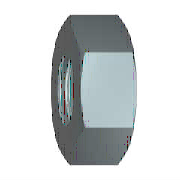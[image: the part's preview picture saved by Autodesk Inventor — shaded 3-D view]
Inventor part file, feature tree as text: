
AUTODESK INVENTOR PART (.ipt)
format: ipt  version: 2017 (Build 210142000, 142)  size: 175,104 bytes
history: native  units: mm (DEFAULTED — no unit token found)
features: sketch x3, chamfer x1, hole x1, other x1, plane x1
ambient origin geometry x7: Origin, YZ Plane, XZ Plane, X Axis, Y Axis, Z Axis, Center Point
bodies: Solid1 (feature_tree), Body (feature_tree)
feature tree (7):
  chamfer  "Chamfer1"  Angle=30.0deg  [1 undecoded]
  hole  "Thread"  [1 undecoded]
  other  "Work Axis1"
  plane  "Work Plane1"
  sketch  "Sketch1"  dims[d0=6.350853mm]
  sketch  "Sketch2"  dims[d1=2.9mm]
  sketch  "Sketch3"  dims[d2=0.0mm d3=30.0deg d4=30.0deg d5=5.5mm d6=5.5mm d7=90.0deg d25=2.459mm d26=6.0mm d27=4.0mm d28=2.0mm d29=14.3117mm d30=8.0mm d31=20.594885mm d8=0.270633mm d9=30.0deg d10=0.270633mm d11=30.0deg d13=0.0mm d14=0.0mm d39=0.0mm d40=0.270633mm d41=0.270633mm d42=0.0mm]
note: 2 required parameter values undecoded (feature->parameter linkage not recoverable at this tier; creation-order binding heuristic only, values carry confidence <= 0.55)
